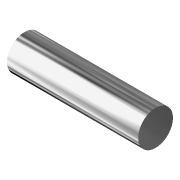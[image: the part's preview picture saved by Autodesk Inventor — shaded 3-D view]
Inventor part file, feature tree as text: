
AUTODESK INVENTOR PART (.ipt)
format: ipt  version: 2022 (Build 260153000, 153)  size: 81,408 bytes
history: native  units: mm
features: extrude x1, sketch x1
ambient origin geometry x8: Origin, YZ Plane, XZ Plane, XY Plane, X Axis, Y Axis, Z Axis, Center Point
bodies: Solid1 (feature_tree)
feature tree (2):
  extrude  "Extrusion1"  Depth=46.0mm TaperAngle=0.0deg
  sketch  "Sketch1"  dims[d0=12.2mm d1=46.0mm d2=0.0mm]
